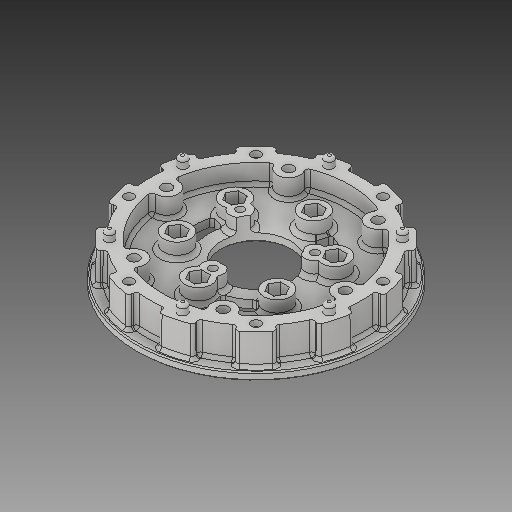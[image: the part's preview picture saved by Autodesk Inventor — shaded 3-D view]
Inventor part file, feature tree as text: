
AUTODESK INVENTOR PART (.ipt)
format: ipt  version: 2019.3 (Build 233278000, 278)  size: 1,541,120 bytes
history: native  units: in
note: dims shown in document units (in); Inventor stores cm internally (conversion verified against a paired STEP export)
features: fillet x1
ambient origin geometry x8: Origin, YZ Plane, XZ Plane, XY Plane, X Axis, Y Axis, Z Axis, Center Point
bodies: Solid1 (feature_tree)
feature tree (1):
  fillet  "Fillet18"  [1 undecoded]
note: 1 required parameter value undecoded (feature->parameter linkage not recoverable at this tier; creation-order binding heuristic only, values carry confidence <= 0.55)
